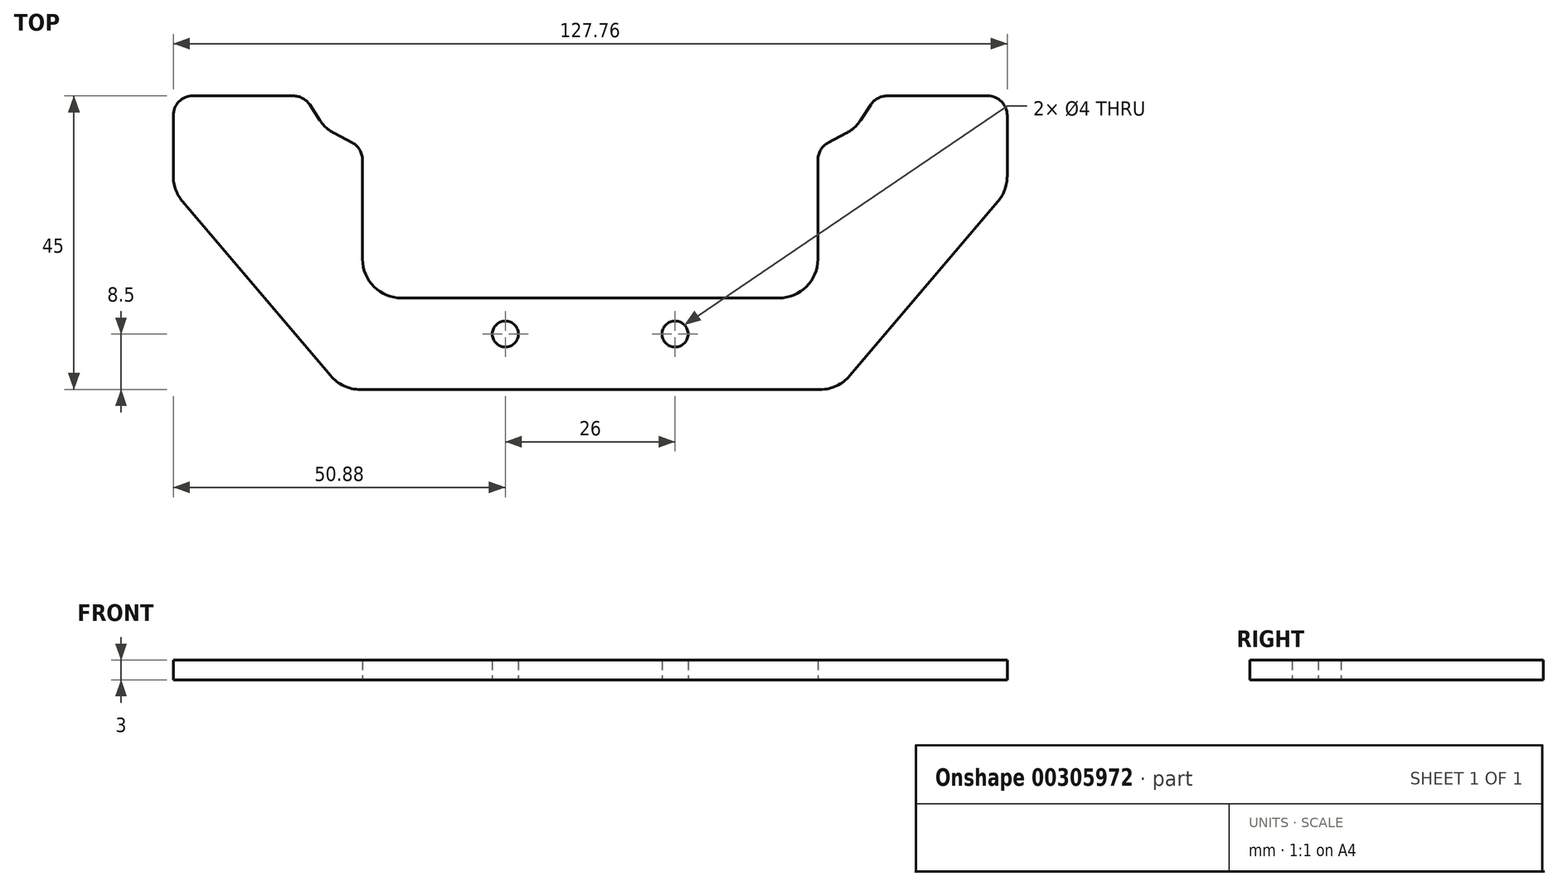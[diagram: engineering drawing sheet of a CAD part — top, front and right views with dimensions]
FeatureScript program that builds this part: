
annotation { "Feature Type Name" : "Feature", "Feature Type Description" : "" }
export const myFeature = defineFeature(function(context is Context, id is Id, definition is map)
    precondition{}
    {
        {
            var Q0;
            Q0=qCreatedBy(makeId("Top.planeOp"),FACE);
            var sketch = newSketch(context, id + "F0", { "sketchPlane" : qUnion([Q0])});
            skLineSegment(sketch, "E0", {"start": v(0, 0) * mm, "end": v(35.22, 0) * mm});
            skLineSegment(sketch, "E1", {"start": v(39.8, 2.12) * mm, "end": v(62.45, 28.82) * mm});
            skLineSegment(sketch, "E2", {"start": v(63.88, 32.7) * mm, "end": v(63.88, 42) * mm});
            skLineSegment(sketch, "E3", {"start": v(60.88, 45) * mm, "end": v(45.5, 45) * mm});
            skLineSegment(sketch, "E4", {"start": v(43, 43.65) * mm, "end": v(41.42, 41.28) * mm});
            skLineSegment(sketch, "E5", {"start": v(39.2, 39.27) * mm, "end": v(36.48, 37.84) * mm});
            skLineSegment(sketch, "E6", {"start": v(34.88, 35.19) * mm, "end": v(34.88, 20) * mm});
            skLineSegment(sketch, "E7", {"start": v(28.88, 14) * mm, "end": v(0, 14) * mm});
            skPoint(sketch, "E8.visualSharp", {"position": v(34.88, 14) * mm});
            skArc(sketch, "E8.filletArc", {"start": v(28.88, 14) * mm, "mid": v(33.12, 15.76) * mm, "end": v(34.88, 20) * mm});
            skPoint(sketch, "E9.visualSharp", {"position": v(34.88, 37) * mm});
            skArc(sketch, "E9.filletArc", {"start": v(36.48, 37.84) * mm, "mid": v(35.31, 36.74) * mm, "end": v(34.88, 35.19) * mm});
            skPoint(sketch, "E10.visualSharp", {"position": v(40.57, 40) * mm});
            skArc(sketch, "E10.filletArc", {"start": v(39.2, 39.27) * mm, "mid": v(40.44, 40.14) * mm, "end": v(41.42, 41.28) * mm});
            skPoint(sketch, "E11.visualSharp", {"position": v(43.88, 45) * mm});
            skArc(sketch, "E11.filletArc", {"start": v(45.5, 45) * mm, "mid": v(44.07, 44.64) * mm, "end": v(43, 43.65) * mm});
            skPoint(sketch, "E12.visualSharp", {"position": v(63.88, 45) * mm});
            skArc(sketch, "E12.filletArc", {"start": v(63.88, 42) * mm, "mid": v(63, 44.12) * mm, "end": v(60.88, 45) * mm});
            skPoint(sketch, "E13.visualSharp", {"position": v(63.88, 30.5) * mm});
            skArc(sketch, "E13.filletArc", {"start": v(62.45, 28.82) * mm, "mid": v(63.51, 30.63) * mm, "end": v(63.88, 32.7) * mm});
            skPoint(sketch, "E14.visualSharp", {"position": v(38, 0) * mm});
            skArc(sketch, "E14.filletArc", {"start": v(35.22, 0) * mm, "mid": v(37.74, 0.56) * mm, "end": v(39.8, 2.12) * mm});
            skLineSegment(sketch, "E15.MirrorCS", {"start": v(-28.88, 14) * mm, "end": v(0, 14) * mm});
            skLineSegment(sketch, "E16.MirrorCS", {"start": v(0, 0) * mm, "end": v(-35.22, 0) * mm});
            skLineSegment(sketch, "E17.MirrorCS", {"start": v(-43, 43.65) * mm, "end": v(-41.42, 41.28) * mm});
            skLineSegment(sketch, "E18.MirrorCS", {"start": v(-39.2, 39.27) * mm, "end": v(-36.48, 37.84) * mm});
            skArc(sketch, "E19.MirrorCS", {"start": v(-39.2, 39.27) * mm, "mid": v(-40.44, 40.14) * mm, "end": v(-41.42, 41.28) * mm});
            skArc(sketch, "E20.MirrorCS", {"start": v(-45.5, 45) * mm, "mid": v(-44.07, 44.64) * mm, "end": v(-43, 43.65) * mm});
            skArc(sketch, "E21.MirrorCS", {"start": v(-36.48, 37.84) * mm, "mid": v(-35.31, 36.74) * mm, "end": v(-34.88, 35.19) * mm});
            skArc(sketch, "E22.MirrorCS", {"start": v(-35.22, 0) * mm, "mid": v(-37.74, 0.56) * mm, "end": v(-39.8, 2.12) * mm});
            skArc(sketch, "E23.MirrorCS", {"start": v(-62.45, 28.82) * mm, "mid": v(-63.51, 30.63) * mm, "end": v(-63.88, 32.7) * mm});
            skArc(sketch, "E24.MirrorCS", {"start": v(-63.88, 42) * mm, "mid": v(-63, 44.12) * mm, "end": v(-60.88, 45) * mm});
            skPoint(sketch, "E25.MirrorP", {"position": v(-40.57, 40) * mm});
            skPoint(sketch, "E26.MirrorP", {"position": v(-38, 0) * mm});
            skLineSegment(sketch, "E27.MirrorCS", {"start": v(-39.8, 2.12) * mm, "end": v(-62.45, 28.82) * mm});
            skPoint(sketch, "E28.MirrorP", {"position": v(-34.88, 37) * mm});
            skLineSegment(sketch, "E29.MirrorCS", {"start": v(-63.88, 32.7) * mm, "end": v(-63.88, 42) * mm});
            skLineSegment(sketch, "E30.MirrorCS", {"start": v(-60.88, 45) * mm, "end": v(-45.5, 45) * mm});
            skPoint(sketch, "E31.MirrorP", {"position": v(-34.88, 14) * mm});
            skPoint(sketch, "E32.MirrorP", {"position": v(-63.88, 30.5) * mm});
            skLineSegment(sketch, "E33.MirrorCS", {"start": v(-34.88, 35.19) * mm, "end": v(-34.88, 20) * mm});
            skArc(sketch, "E34.MirrorCS", {"start": v(-28.88, 14) * mm, "mid": v(-33.12, 15.76) * mm, "end": v(-34.88, 20) * mm});
            skPoint(sketch, "E35.MirrorP", {"position": v(-43.88, 45) * mm});
            skPoint(sketch, "E36.MirrorP", {"position": v(-63.88, 45) * mm});
            skCircle(sketch, "E37", {"center": v(13, 8.5) * mm, "radius": 2 * mm});
            skCircle(sketch, "E38.MirrorC", {"center": v(-13, 8.5) * mm, "radius": 2 * mm});
            skSolve(sketch);
        }
        {
            var Q0;
            Q0=makeQuery(id+"F0.imprint","IMPRINT",FACE,{"disambiguationData":[TD([[makeQuery(id+"F0.imprint","IMPRINT",EDGE,{"derivedFrom":sQuery(id+"F0.wireOp",EDGE,"E0")}),1.0]])]});
            extrude(context, id + "F1", {"entities" : qUnion([Q0]), "depth" : 3 * mm});
        }
    });
